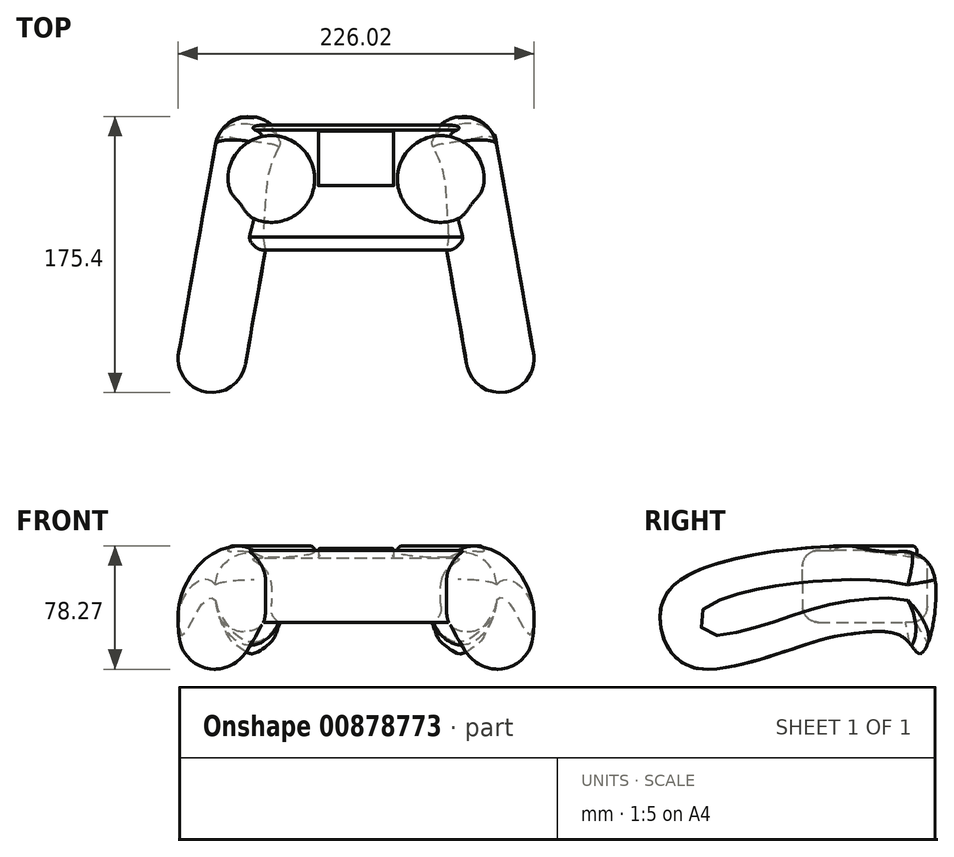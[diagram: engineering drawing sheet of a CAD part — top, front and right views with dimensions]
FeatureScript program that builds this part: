
annotation { "Feature Type Name" : "Feature", "Feature Type Description" : "" }
export const myFeature = defineFeature(function(context is Context, id is Id, definition is map)
    precondition{}
    {
        {
            var Q0;
            Q0=qCreatedBy(makeId("Right.planeOp"),FACE);
            var sketch = newSketch(context, id + "F0", { "sketchPlane" : qUnion([Q0])});
            skLineSegment(sketch, "E0.bottom", {"start": v(-0.34, 22.65) * mm, "end": v(-31.6, 22.65) * mm});
            skLineSegment(sketch, "E0.top", {"start": v(29.32, -22.8) * mm, "end": v(-29.85, -22.8) * mm});
            skLineSegment(sketch, "E0.left", {"start": v(39.32, 13.24) * mm, "end": v(39.32, -12.8) * mm});
            skLineSegment(sketch, "E0.right", {"start": v(-39.85, 12.8) * mm, "end": v(-39.85, -12.8) * mm});
            skPoint(sketch, "E0.middle", {"position": v(-0.26, 0) * mm});
            skPoint(sketch, "E1.visualSharp", {"position": v(39.32, 22.8) * mm});
            skPoint(sketch, "E2.visualSharp", {"position": v(-39.85, 22.8) * mm});
            skArc(sketch, "E2.filletArc", {"start": v(-31.6, 22.65) * mm, "mid": v(-37.52, 19.22) * mm, "end": v(-39.85, 12.8) * mm});
            skPoint(sketch, "E3.visualSharp", {"position": v(-39.85, -22.8) * mm});
            skArc(sketch, "E3.filletArc", {"start": v(-39.85, -12.8) * mm, "mid": v(-36.92, -19.87) * mm, "end": v(-29.85, -22.8) * mm});
            skPoint(sketch, "E4.visualSharp", {"position": v(39.32, -22.8) * mm});
            skArc(sketch, "E4.filletArc", {"start": v(29.32, -22.8) * mm, "mid": v(36.39, -19.87) * mm, "end": v(39.32, -12.8) * mm});
            skPoint(sketch, "E5", {"position": v(39.32, 16.77) * mm});
            skArc(sketch, "E6.filletArc", {"start": v(39.32, 13.24) * mm, "mid": v(38.52, 15.94) * mm, "end": v(36.4, 17.78) * mm});
            skLineSegment(sketch, "E7", {"start": v(1, 22.56) * mm, "end": v(36.4, 17.78) * mm});
            skPoint(sketch, "E8.visualSharp", {"position": v(0.34, 22.65) * mm});
            skArc(sketch, "E8.filletArc", {"start": v(1, 22.56) * mm, "mid": v(0.33, 22.63) * mm, "end": v(-0.34, 22.65) * mm});
            skSolve(sketch);
        }
        {
            var Q0;
            Q0=makeQuery(id+"F0.imprint","IMPRINT",FACE,{"disambiguationData":[TD([[makeQuery(id+"F0.imprint","IMPRINT",EDGE,{"derivedFrom":sQuery(id+"F0.wireOp",EDGE,"E0.bottom")}),1.0]])]});
            extrude(context, id + "F1", {"entities" : qUnion([Q0]), "depth" : 70 * mm, "offsetDistance" : 25 * mm});
        }
        {
            var Q0;
            Q0=qCreatedBy(makeId("Right.planeOp"),FACE);
            var sketch = newSketch(context, id + "F2", { "sketchPlane" : qUnion([Q0])});
            skFitSpline(sketch, "E9.MirrorC", {"points": [v(55.08, 13) * mm, v(30.49, 28.5) * mm, v(-25.46, 29.48) * mm, v(-112.42, 5.26) * mm, v(-119.27, -25.3) * mm, v(-104.57, -44.72) * mm, v(-69.52, -44.76) * mm, v(-17.05, -28.86) * mm, v(2.78, -25.17) * mm, v(36.25, -27.51) * mm, v(47.23, -37.65) * mm, v(55.08, 13) * mm]});
            skSolve(sketch);
        }
        {
            var Q0;
            Q0=makeQuery(id+"F2.imprint","IMPRINT",FACE,{"disambiguationData":[TD([[makeQuery(id+"F2.imprint","IMPRINT",EDGE,{"derivedFrom":sQuery(id+"F2.wireOp",EDGE,"E9.MirrorC")}),1.0]])]});
            extrude(context, id + "F3", {"entities" : qUnion([Q0]), "depth" : 43 * mm, "offsetDistance" : 25 * mm});
        }
        {
            var Q0;
            Q0=makeQuery(id+"F3.opExtrude","SWEPT_BODY",BODY,{"disambiguationData":[OSD([sQuery(id+"F2.wireOp",EDGE,"E9.MirrorC")])]});
            transform(context, id + "F4", {"entities" : qUnion([Q0]), "transformType" : TransformType.TRANSLATION_3D, "dx" : 45 * mm, "dy" : -171 * mm, "dz" : -67 * mm, "makeCopy" : false});
        }
        {
            var Q0;
            Q0=makeQuery(id+"F3.opExtrude","SWEPT_BODY",BODY,{"disambiguationData":[OSD([sQuery(id+"F2.wireOp",EDGE,"E9.MirrorC")])]});
            transform(context, id + "F5", {"entities" : qUnion([Q0]), "transformType" : TransformType.TRANSLATION_3D, "dx" : 0 * mm, "dy" : 160 * mm, "dz" : 62 * mm, "makeCopy" : false});
        }
        {
            var Q0;
            Q0=makeQuery(id+"F3.opExtrude","SWEPT_FACE",FACE,{"disambiguationData":[OSD([sQuery(id+"F2.wireOp",EDGE,"E9.MirrorC")])]});
            fillet(context, id + "F6", {"entities" : qUnion([Q0]), "radius" : 21.3 * mm, "tangentPropagation" : true, "allowEdgeOverflow" : false});
        }
        {
            var Q0;
            Q0=makeQuery(id+"F1.opExtrude","CAP_EDGE",EDGE,{"disambiguationData":[OSD([sQuery(id+"F0.wireOp",EDGE,"E0.bottom")])],"isStart":false});
            fillet(context, id + "F7", {"entities" : qUnion([Q0]), "radius" : 3 * mm, "tangentPropagation" : true, "allowEdgeOverflow" : false});
        }
        {
            var Q0;
            Q0=qCreatedBy(makeId("Right.planeOp"),FACE);
            cPlane(context, id + "F8", {"entities" : qUnion([Q0]), "cplaneType" : CPlaneType.OFFSET, "offset" : 71 * mm, "width" : 150 * mm, "height" : 150 * mm});
        }
        {
            var Q0;
            Q0=qCreatedBy(id+"F8.planeOp",FACE);
            var sketch = newSketch(context, id + "F9", { "sketchPlane" : qUnion([Q0])});
            skLineSegment(sketch, "E10", {"start": v(33.14, 61.33) * mm, "end": v(33.14, -63.6) * mm});
            skSolve(sketch);
        }
        {
            var Q0;
            Q0=makeQuery(id+"F3.opExtrude","SWEPT_BODY",BODY,{"disambiguationData":[OSD([sQuery(id+"F2.wireOp",EDGE,"E9.MirrorC")])]});
            var Q1;
            Q1=sQuery(id+"F9.wireOp",EDGE,"E10");
            transform(context, id + "F10", {"entities" : qUnion([Q0]), "transformType" : TransformType.ROTATION, "transformAxis" : qUnion([Q1]), "angle" : 10 * degree, "oppositeDirection" : true, "makeCopy" : false});
        }
        {
            var Q0;
            {var subQ0=makeQuery(id+"F1.opExtrude","SWEPT_FACE",FACE,{"disambiguationData":[OSD([sQuery(id+"F0.wireOp",EDGE,"E0.bottom")])]});Q0=makeQuery(id+"F19.boolean.opBoolean","MERGE",FACE,{"derivedFrom":[subQ0,makeQuery(id+"F19.opPattern","COPY",FACE,{"derivedFrom":subQ0,"instanceName":"1"})]});}
            cPlane(context, id + "F11", {"entities" : qUnion([Q0]), "cplaneType" : CPlaneType.OFFSET, "offset" : 3 * mm, "width" : 150 * mm, "height" : 150 * mm});
        }
        {
            var Q0;
            Q0=qCreatedBy(id+"F11.planeOp",FACE);
            var sketch = newSketch(context, id + "F12", { "sketchPlane" : qUnion([Q0])});
            skCircle(sketch, "E11", {"center": v(53.8, 5.18) * mm, "radius": 27.55 * mm});
            skSolve(sketch);
        }
        {
            var Q0;
            Q0=makeQuery(id+"F12.imprint","IMPRINT",FACE,{"disambiguationData":[TD([[makeQuery(id+"F12.imprint","IMPRINT",EDGE,{"derivedFrom":sQuery(id+"F12.wireOp",EDGE,"E11")}),1.0]])]});
            extrude(context, id + "F13", {"entities" : qUnion([Q0]), "oppositeDirection" : true, "depth" : 10 * mm, "offsetDistance" : 25 * mm});
        }
        {
            var Q0;
            Q0=makeQuery(id+"F13.opExtrude","CAP_EDGE",EDGE,{"disambiguationData":[OSD([sQuery(id+"F12.wireOp",EDGE,"E11")])],"isStart":true});
            fillet(context, id + "F14", {"entities" : qUnion([Q0]), "radius" : 3 * mm, "tangentPropagation" : true, "allowEdgeOverflow" : false});
        }
        {
            var Q0;
            {var subQ0=makeQuery(id+"F1.opExtrude","SWEPT_FACE",FACE,{"disambiguationData":[OSD([sQuery(id+"F0.wireOp",EDGE,"E7")])]});Q0=makeQuery(id+"F19.boolean.opBoolean","MERGE",FACE,{"derivedFrom":[subQ0,makeQuery(id+"F19.opPattern","COPY",FACE,{"derivedFrom":subQ0,"instanceName":"1"})]});}
            cPlane(context, id + "F15", {"entities" : qUnion([Q0]), "cplaneType" : CPlaneType.OFFSET, "offset" : 1.5 * mm, "width" : 150 * mm, "height" : 150 * mm});
        }
        {
            var Q0;
            Q0=qCreatedBy(id+"F15.planeOp",FACE);
            var sketch = newSketch(context, id + "F16", { "sketchPlane" : qUnion([Q0])});
            skLineSegment(sketch, "E12.bottom", {"start": v(0, -2.12) * mm, "end": v(23.91, -2.12) * mm});
            skLineSegment(sketch, "E12.top", {"start": v(0, 32.95) * mm, "end": v(23.91, 32.95) * mm});
            skLineSegment(sketch, "E12.left", {"start": v(0, -2.12) * mm, "end": v(0, 32.95) * mm});
            skLineSegment(sketch, "E12.right", {"start": v(23.91, -2.12) * mm, "end": v(23.91, 32.95) * mm});
            skSolve(sketch);
        }
        {
            var Q0;
            Q0=makeQuery(id+"F16.imprint","IMPRINT",FACE,{"disambiguationData":[TD([[makeQuery(id+"F16.imprint","IMPRINT",EDGE,{"derivedFrom":sQuery(id+"F16.wireOp",EDGE,"E12.bottom")}),1.0]])]});
            extrude(context, id + "F17", {"entities" : qUnion([Q0]), "operationType" : NewBodyOperationType.ADD, "oppositeDirection" : true, "depth" : 5 * mm, "offsetDistance" : 25 * mm});
        }
        {
            var Q0;
            Q0=makeQuery(id+"F17.opExtrude","CAP_EDGE",EDGE,{"disambiguationData":[OSD([sQuery(id+"F16.wireOp",EDGE,"E12.right")])],"isStart":true});
            var Q1;
            Q1=makeQuery(id+"F17.opExtrude","CAP_EDGE",EDGE,{"disambiguationData":[OSD([sQuery(id+"F16.wireOp",EDGE,"E12.bottom")])],"isStart":true});
            var Q2;
            Q2=makeQuery(id+"F17.opExtrude","CAP_EDGE",EDGE,{"disambiguationData":[OSD([sQuery(id+"F16.wireOp",EDGE,"E12.top")])],"isStart":true});
            fillet(context, id + "F18", {"entities" : qUnion([Q0, Q1, Q2]), "radius" : 1 * mm, "tangentPropagation" : true, "allowEdgeOverflow" : false});
        }
        {
            var Q0;
            Q0=makeQuery(id+"F1.opExtrude","SWEPT_BODY",BODY,{"disambiguationData":[OSD([sQuery(id+"F0.wireOp",EDGE,"E0.bottom"),sQuery(id+"F0.wireOp",EDGE,"E0.top"),sQuery(id+"F0.wireOp",EDGE,"E0.left"),sQuery(id+"F0.wireOp",EDGE,"E0.right"),sQuery(id+"F0.wireOp",EDGE,"E2.filletArc"),sQuery(id+"F0.wireOp",EDGE,"E3.filletArc"),sQuery(id+"F0.wireOp",EDGE,"E4.filletArc"),sQuery(id+"F0.wireOp",EDGE,"E6.filletArc"),sQuery(id+"F0.wireOp",EDGE,"E7"),sQuery(id+"F0.wireOp",EDGE,"E8.filletArc")])]});
            var Q1;
            Q1=makeQuery(id+"F3.opExtrude","SWEPT_BODY",BODY,{"disambiguationData":[OSD([sQuery(id+"F2.wireOp",EDGE,"E9.MirrorC")])]});
            var Q2;
            Q2=makeQuery(id+"F13.opExtrude","SWEPT_BODY",BODY,{"disambiguationData":[OSD([sQuery(id+"F12.wireOp",EDGE,"E11")])]});
            var Q3;
            Q3=qCreatedBy(makeId("Right.planeOp"),FACE);
            mirror(context, id + "F19", {"operationType" : NewBodyOperationType.ADD, "entities" : qUnion([Q0, Q1, Q2]), "mirrorPlane" : qUnion([Q3])});
        }
        {
            var Q0;
            Q0=makeQuery(id+"F13.opExtrude","CAP_FACE",FACE,{"disambiguationData":[OSD([sQuery(id+"F12.wireOp",EDGE,"E11")])],"isStart":true});
            var sketch = newSketch(context, id + "F20", { "sketchPlane" : qUnion([Q0])});
            skLineSegment(sketch, "E13", {"start": v(53.7, 29.73) * mm, "end": v(53.7, -19.37) * mm, "construction": true});
            skLineSegment(sketch, "E14", {"start": v(78.35, 5.18) * mm, "end": v(29.24, 5.18) * mm, "construction": true});
            skCircle(sketch, "E15", {"center": v(53.7, 18.18) * mm, "radius": 7 * mm});
            skSolve(sketch);
        }
        {
            var Q0;
            Q0=sQuery(id+"F20.wireOp",EDGE,"E15");
            extrude(context, id + "F21", {"bodyType" : ToolBodyType.SURFACE, "surfaceEntities" : qUnion([Q0]), "depth" : 2 * mm, "offsetDistance" : 25 * mm});
        }
    });
